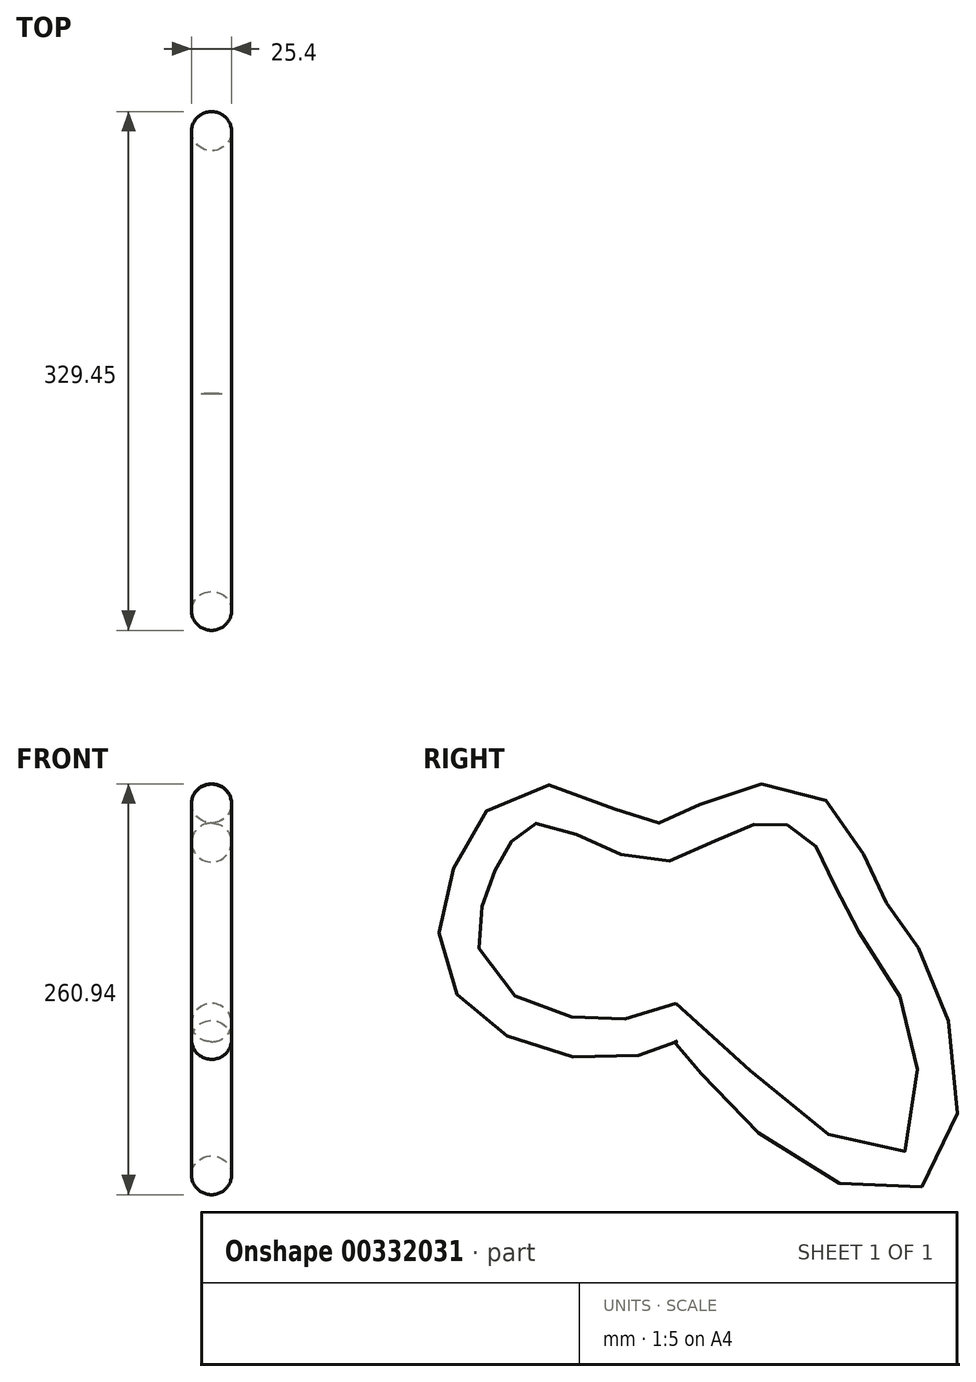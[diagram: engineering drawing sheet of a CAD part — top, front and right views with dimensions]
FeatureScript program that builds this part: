
annotation { "Feature Type Name" : "Feature", "Feature Type Description" : "" }
export const myFeature = defineFeature(function(context is Context, id is Id, definition is map)
    precondition{}
    {
        {
            var Q0;
            Q0=qCreatedBy(makeId("Front.planeOp"),FACE);
            var sketch = newSketch(context, id + "F0", { "sketchPlane" : qUnion([Q0])});
            skCircle(sketch, "E0", {"center": v(0, 0) * mm, "radius": 12.7 * mm});
            skSolve(sketch);
        }
        {
            var Q0;
            Q0=qCreatedBy(makeId("Right.planeOp"),FACE);
            var sketch = newSketch(context, id + "F1", { "sketchPlane" : qUnion([Q0])});
            skFitSpline(sketch, "E1", {"points": [v(0, 0) * mm, v(-25.9, -7.98) * mm, v(-94.76, 0) * mm, v(-135.75, 39.6) * mm, v(-126.1, 102.8) * mm, v(-87.02, 139.62) * mm, v(-14.21, 115.25) * mm, v(34.48, 135.01) * mm, v(89.16, 130.68) * mm, v(120.27, 74.91) * mm, v(155.19, 18.22) * mm, v(151.94, -91.47) * mm, v(50.27, -51.01) * mm, v(0, 0) * mm]});
            skSolve(sketch);
        }
        {
            var Q0;
            Q0 = qSketchRegion(id + "F0", true);
            var Q1;
            Q1 = qConstructionFilter(qBodyType(qCreatedBy(id + "F1" ,EDGE), BodyType.WIRE), ConstructionObject.NO);
            sweep(context, id + "F2", {"profiles" : qUnion([Q0]), "path" : qUnion([Q1])});
        }
    });
